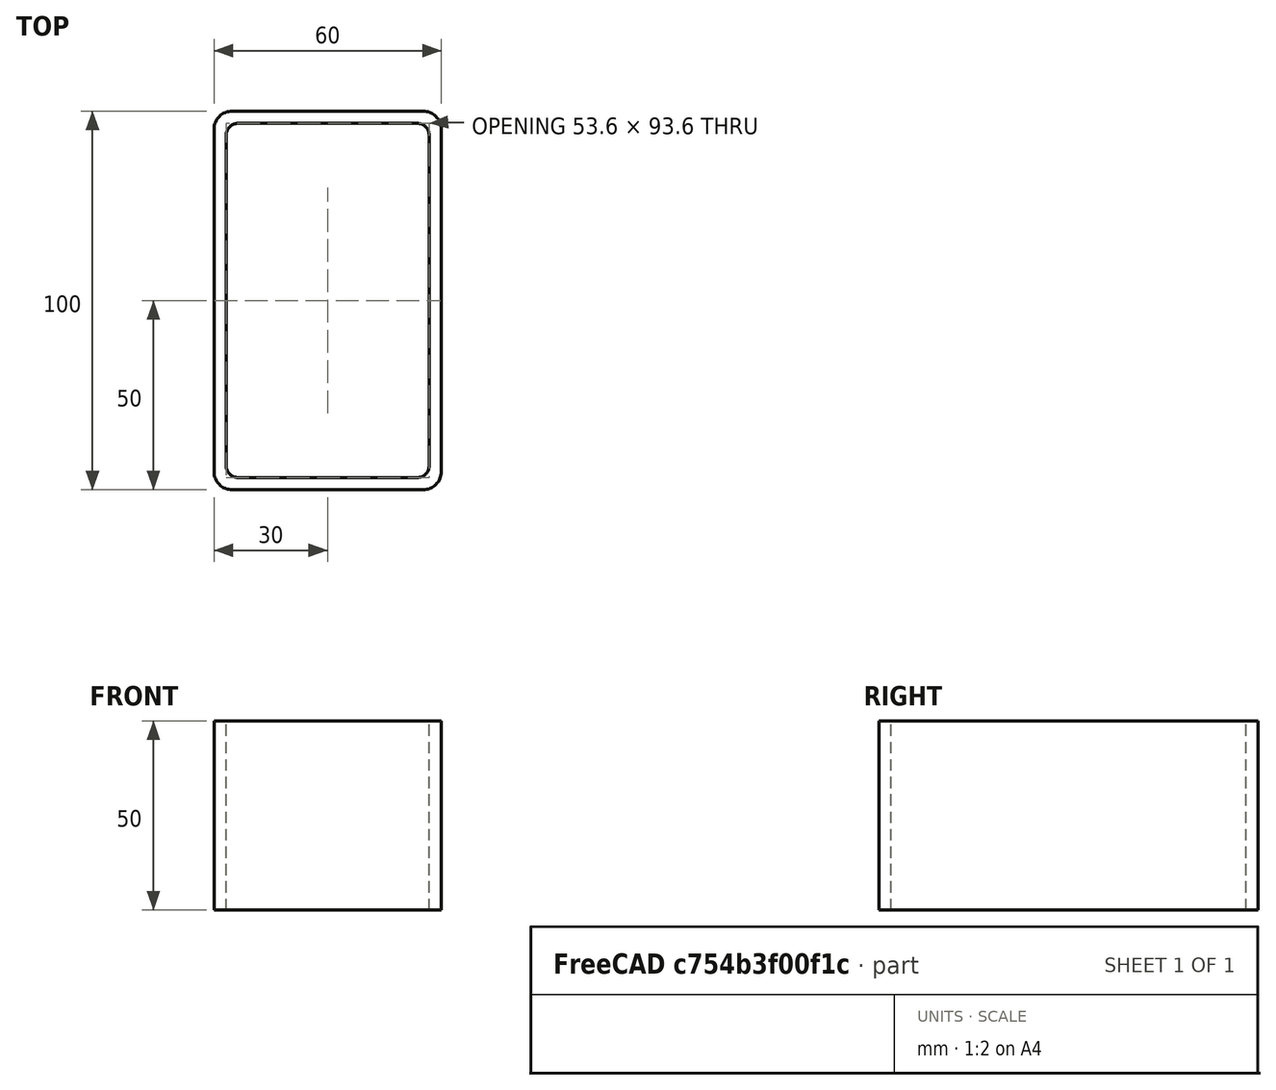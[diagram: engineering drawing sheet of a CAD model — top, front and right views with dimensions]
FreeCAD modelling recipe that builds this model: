
FCSTD DOCUMENT  (FreeCAD 0.15R4671 (Git))
Label: Rectangular hollow section 100x60x3.2 EN10219 S235JRH
License: All rights reserved
LicenseURL: http://en.wikipedia.org/wiki/All_rights_reserved
objects: Sketcher::SketchObject×1, Part::Extrusion×1
note: 2 computed .brp shape members not serialized (recipe doc carries the construction recipe); baked Part::Feature solids carry a one-line shape summary decoded from their .brp

FEATURE [Sketcher::SketchObject] Sketch
  sketch-geometry (16):
    g0: LineSegment StartX=-23.6 StartY=46.8 StartZ=0 EndX=23.6 EndY=46.8 EndZ=0
    g1: LineSegment StartX=26.8 StartY=43.6 StartZ=0 EndX=26.8 EndY=-43.6 EndZ=0
    g2: LineSegment StartX=23.6 StartY=-46.8 StartZ=0 EndX=-23.6 EndY=-46.8 EndZ=0
    g3: LineSegment StartX=-26.8 StartY=-43.6 StartZ=0 EndX=-26.8 EndY=43.6 EndZ=0
    g4: LineSegment StartX=-25.2 StartY=50 StartZ=0 EndX=25.2 EndY=50 EndZ=0
    g5: LineSegment StartX=30 StartY=45.2 StartZ=0 EndX=30 EndY=-45.2 EndZ=0
    g6: LineSegment StartX=25.2 StartY=-50 StartZ=0 EndX=-25.2 EndY=-50 EndZ=0
    g7: LineSegment StartX=-30 StartY=-45.2 StartZ=0 EndX=-30 EndY=45.2 EndZ=0
    g8: ArcOfCircle CenterX=-23.6 CenterY=43.6 CenterZ=0 NormalX=0 NormalY=0 NormalZ=1 Radius=3.2 StartAngle=1.5708 EndAngle=3.14159
    g9: ArcOfCircle CenterX=23.6 CenterY=43.6 CenterZ=0 NormalX=0 NormalY=0 NormalZ=1 Radius=3.2 StartAngle=0 EndAngle=1.5708
    g10: ArcOfCircle CenterX=23.6 CenterY=-43.6 CenterZ=0 NormalX=0 NormalY=0 NormalZ=1 Radius=3.2 StartAngle=4.71239 EndAngle=6.28319
    g11: ArcOfCircle CenterX=-23.6 CenterY=-43.6 CenterZ=0 NormalX=0 NormalY=0 NormalZ=1 Radius=3.2 StartAngle=3.14159 EndAngle=4.71239
    g12: ArcOfCircle CenterX=25.2 CenterY=45.2 CenterZ=0 NormalX=0 NormalY=0 NormalZ=1 Radius=4.8 StartAngle=0 EndAngle=1.5708
    g13: ArcOfCircle CenterX=25.2 CenterY=-45.2 CenterZ=0 NormalX=0 NormalY=0 NormalZ=1 Radius=4.8 StartAngle=4.71239 EndAngle=6.28319
    g14: ArcOfCircle CenterX=-25.2 CenterY=-45.2 CenterZ=0 NormalX=0 NormalY=0 NormalZ=1 Radius=4.8 StartAngle=3.14159 EndAngle=4.71239
    g15: ArcOfCircle CenterX=-25.2 CenterY=45.2 CenterZ=0 NormalX=0 NormalY=0 NormalZ=1 Radius=4.8 StartAngle=1.5708 EndAngle=3.14159
  constraints (36):
    c: Horizontal(g2)
    c: Vertical(g3)
    c: Horizontal(g6)
    c: Vertical(g7)
    c: Tangent(g3,g8) = 1.5708
    c: Tangent(g0,g8) = 1.5708
    c: Tangent(g0,g9) = 1.5708
    c: Tangent(g1,g9) = 1.5708
    c: Tangent(g1,g10) = 1.5708
    c: Tangent(g2,g10) = 1.5708
    c: Tangent(g2,g11) = 1.5708
    c: Tangent(g3,g11) = 1.5708
    c: Tangent(g4,g12) = 1.5708
    c: Tangent(g5,g12) = 1.5708
    c: Tangent(g5,g13) = 1.5708
    c: Tangent(g6,g13) = 1.5708
    c: Tangent(g6,g14) = 1.5708
    c: Tangent(g7,g14) = 1.5708
    c: Tangent(g7,g15) = 1.5708
    c: Tangent(g4,g15) = 1.5708
    c: Equal(g9,g8)
    c: Equal(g9,g11)
    c: Equal(g9,g10)
    c: Equal(g12,g15)
    c: Equal(g12,g14)
    c: Equal(g12,g13)
    c: Symmetric(g4,g6,g-1)
    c: Symmetric(g7,g5,g-2)
    c: DistanceY(g4,g6) = -100
    c: DistanceX(g7,g5) = 60
    c: Symmetric(g3,g1,g-2)
    c: Symmetric(g0,g2,g-1)
    c: DistanceY(g0,g4) = 3.2
    c: DistanceX(g5,g1) = -3.2
    c: Radius(g9) = 3.2
    c: Radius(g12) = 4.8
FEATURE [Part::Extrusion] Extrude  label="Rectangular hollow section 100x60x3.2 EN10219 S235JRH"
  Base = -> Sketch
  Dir = (0,0,50)
  Solid = true
